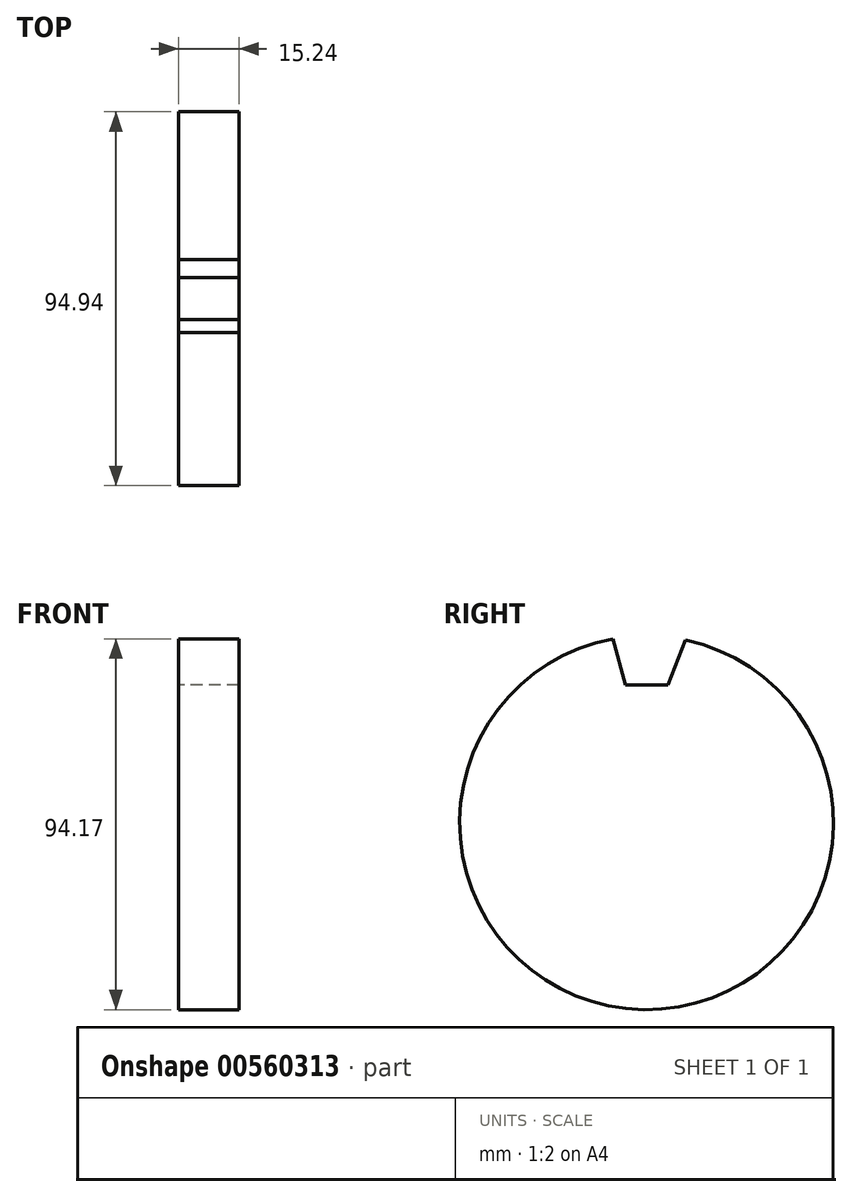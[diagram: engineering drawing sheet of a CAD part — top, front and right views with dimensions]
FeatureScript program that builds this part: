
annotation { "Feature Type Name" : "Feature", "Feature Type Description" : "" }
export const myFeature = defineFeature(function(context is Context, id is Id, definition is map)
    precondition{}
    {
        {
            var Q0;
            Q0=qCreatedBy(makeId("Right.planeOp"),FACE);
            var sketch = newSketch(context, id + "F0", { "sketchPlane" : qUnion([Q0])});
            skCircle(sketch, "E0", {"center": v(0, 0) * mm, "radius": 47.47 * mm});
            skSolve(sketch);
        }
        {
            var Q0;
            Q0=makeQuery(id+"F0.imprint","IMPRINT",FACE,{"disambiguationData":[TD([[makeQuery(id+"F0.imprint","IMPRINT",EDGE,{"derivedFrom":sQuery(id+"F0.wireOp",EDGE,"E0")}),1.0]])]});
            extrude(context, id + "F1", {"entities" : qUnion([Q0]), "depth" : 7.62 * mm, "offsetDistance" : 25.4 * mm, "hasSecondDirection" : true, "secondDirectionOppositeDirection" : true, "secondDirectionDepth" : 7.62 * mm});
        }
        {
            var Q0;
            Q0=makeQuery(id+"F1.opExtrude","CAP_FACE",FACE,{"disambiguationData":[OSD([sQuery(id+"F0.wireOp",EDGE,"E0")])],"isStart":false});
            var sketch = newSketch(context, id + "F2", { "sketchPlane" : qUnion([Q0])});
            skLineSegment(sketch, "E1", {"start": v(0, 35.04) * mm, "end": v(5.39, 35.04) * mm});
            skLineSegment(sketch, "E2", {"start": v(5.39, 35.04) * mm, "end": v(11.57, 50.5) * mm});
            skLineSegment(sketch, "E3", {"start": v(11.57, 50.5) * mm, "end": v(-9.6, 50.5) * mm});
            skLineSegment(sketch, "E4", {"start": v(-9.6, 50.5) * mm, "end": v(-5.31, 35.04) * mm});
            skLineSegment(sketch, "E5", {"start": v(-5.31, 35.04) * mm, "end": v(0, 35.04) * mm});
            skSolve(sketch);
        }
        {
            var Q0;
            {var subQ2=sQuery(id+"F2.wireOp",EDGE,"E1");Q0=makeQuery(id+"F2.imprint","IMPRINT",FACE,{"disambiguationData":[TD([[makeQuery(id+"F2.imprint","IMPRINT",EDGE,{"derivedFrom":subQ2}),1.0]])]});}
            var Q1;
            {var subQ0=sQuery(id+"F2.wireOp",EDGE,"E3");Q1=makeQuery(id+"F2.imprint","IMPRINT",FACE,{"disambiguationData":[TD([[makeQuery(id+"F2.imprint","IMPRINT",EDGE,{"derivedFrom":subQ0}),1.0]])]});}
            extrude(context, id + "F3", {"entities" : qUnion([Q0, Q1]), "operationType" : NewBodyOperationType.REMOVE, "depth" : 25.4 * mm, "offsetDistance" : 25.4 * mm, "hasSecondDirection" : true, "secondDirectionOppositeDirection" : true, "secondDirectionDepth" : 25.4 * mm});
        }
    });
